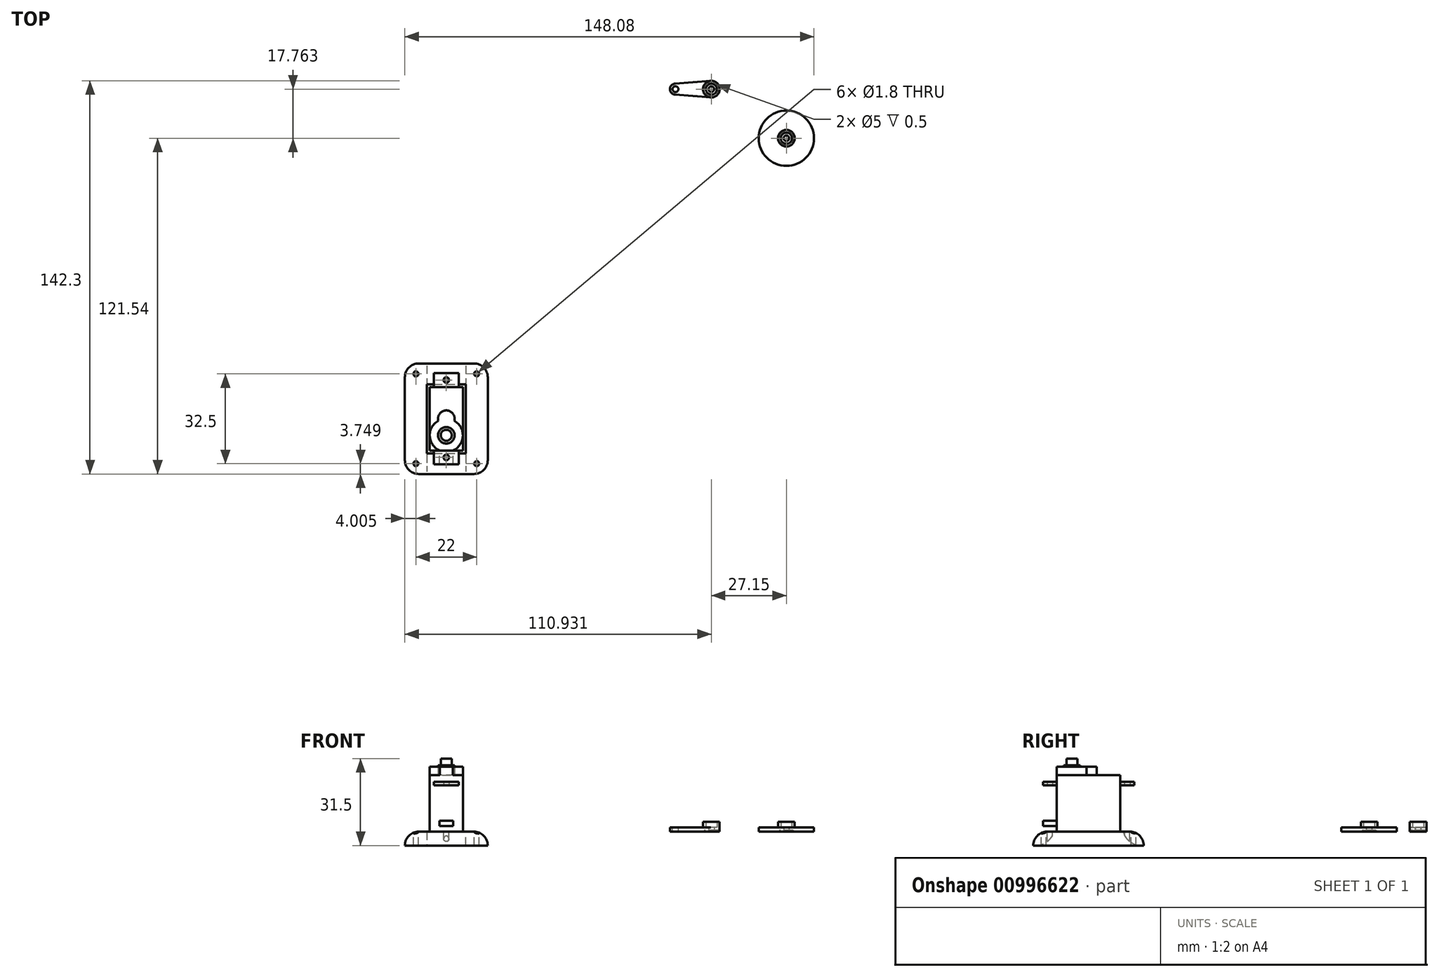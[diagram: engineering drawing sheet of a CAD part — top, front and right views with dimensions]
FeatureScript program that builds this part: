
annotation { "Feature Type Name" : "Feature", "Feature Type Description" : "" }
export const myFeature = defineFeature(function(context is Context, id is Id, definition is map)
    precondition{}
    {
        {
            var Q0;
            Q0=qCreatedBy(makeId("Top.planeOp"),FACE);
            var sketch = newSketch(context, id + "F0", { "sketchPlane" : qUnion([Q0])});
            skLineSegment(sketch, "E0.bottom", {"start": v(-62.64, -62.96) * mm, "end": v(-50.64, -62.96) * mm});
            skLineSegment(sketch, "E0.top", {"start": v(-62.64, -39.96) * mm, "end": v(-50.64, -39.96) * mm});
            skLineSegment(sketch, "E0.left", {"start": v(-62.64, -62.96) * mm, "end": v(-62.64, -39.96) * mm});
            skLineSegment(sketch, "E0.right", {"start": v(-50.64, -62.96) * mm, "end": v(-50.64, -39.96) * mm});
            skSolve(sketch);
        }
        {
            var Q0;
            Q0=makeQuery(id+"F0.imprint","IMPRINT",FACE,{"disambiguationData":[TD([[makeQuery(id+"F0.imprint","IMPRINT",EDGE,{"derivedFrom":sQuery(id+"F0.wireOp",EDGE,"E0.bottom")}),1.0]])]});
            extrude(context, id + "F1", {"entities" : qUnion([Q0]), "depth" : 20.5 * mm, "offsetDistance" : 25 * mm});
        }
        {
            var Q0;
            Q0=makeQuery(id+"F1.opExtrude","CAP_FACE",FACE,{"disambiguationData":[OSD([sQuery(id+"F0.wireOp",EDGE,"E0.bottom"),sQuery(id+"F0.wireOp",EDGE,"E0.top"),sQuery(id+"F0.wireOp",EDGE,"E0.left"),sQuery(id+"F0.wireOp",EDGE,"E0.right")])],"isStart":false});
            var sketch = newSketch(context, id + "F2", { "sketchPlane" : qUnion([Q0])});
            skLineSegment(sketch, "E1", {"start": v(-56.64, -39.96) * mm, "end": v(-56.64, -62.96) * mm, "construction": true});
            skCircle(sketch, "E2", {"center": v(-56.64, -57.46) * mm, "radius": 6 * mm});
            skArc(sketch, "E3", {"start": v(-53.73, -52.21) * mm, "mid": v(-56.64, -48.46) * mm, "end": v(-59.54, -52.21) * mm});
            skSolve(sketch);
        }
        {
            var Q0;
            {var subQ0=sQuery(id+"F2.wireOp",EDGE,"E2");var subQ4=sQuery(id+"F2.wireOp",EDGE,"E3");var subQ6=makeQuery(id+"F2.imprint","INTERSECT",VERTEX,{"disambiguationData":[OD(0.0)],"derivedFrom":[subQ0,subQ4]});Q0=makeQuery(id+"F2.imprint","IMPRINT",FACE,{"disambiguationData":[TD([[makeQuery(id+"F2.imprint","IMPRINT",EDGE,{"disambiguationData":[TD([[subQ6,1.0]])],"derivedFrom":subQ0}),1.0]])]});}
            var Q1;
            {var subQ0=sQuery(id+"F2.wireOp",EDGE,"E3");Q1=makeQuery(id+"F2.imprint","IMPRINT",FACE,{"disambiguationData":[TD([[makeQuery(id+"F2.imprint","IMPRINT",EDGE,{"derivedFrom":subQ0}),1.0]])]});}
            extrude(context, id + "F3", {"entities" : qUnion([Q0, Q1]), "operationType" : NewBodyOperationType.ADD, "depth" : 3 * mm, "offsetDistance" : 25 * mm});
        }
        {
            var Q0;
            Q0=makeQuery(id+"F3.opExtrude","CAP_FACE",FACE,{"disambiguationData":[OSD([sQuery(id+"F0.wireOp",EDGE,"E0.bottom"),sQuery(id+"F2.wireOp",EDGE,"E2"),sQuery(id+"F2.wireOp",EDGE,"E3")])],"isStart":false});
            var sketch = newSketch(context, id + "F4", { "sketchPlane" : qUnion([Q0])});
            skCircle(sketch, "E4", {"center": v(-56.64, -57.46) * mm, "radius": 3 * mm});
            skSolve(sketch);
        }
        {
            var Q0;
            Q0=makeQuery(id+"F4.imprint","IMPRINT",FACE,{"disambiguationData":[TD([[makeQuery(id+"F4.imprint","IMPRINT",EDGE,{"derivedFrom":sQuery(id+"F4.wireOp",EDGE,"E4")}),1.0]])]});
            extrude(context, id + "F5", {"entities" : qUnion([Q0]), "operationType" : NewBodyOperationType.ADD, "depth" : 0.5 * mm, "offsetDistance" : 25 * mm});
        }
        {
            var Q0;
            Q0=makeQuery(id+"F5.opExtrude","CAP_FACE",FACE,{"disambiguationData":[OSD([sQuery(id+"F4.wireOp",EDGE,"E4")])],"isStart":false});
            var sketch = newSketch(context, id + "F6", { "sketchPlane" : qUnion([Q0])});
            skCircle(sketch, "E5", {"center": v(-56.64, -57.46) * mm, "radius": 2 * mm});
            skSolve(sketch);
        }
        {
            var Q0;
            Q0=makeQuery(id+"F6.imprint","IMPRINT",FACE,{"disambiguationData":[TD([[makeQuery(id+"F6.imprint","IMPRINT",EDGE,{"derivedFrom":sQuery(id+"F6.wireOp",EDGE,"E5")}),1.0]])]});
            extrude(context, id + "F7", {"entities" : qUnion([Q0]), "operationType" : NewBodyOperationType.ADD, "depth" : 2.5 * mm, "offsetDistance" : 25 * mm});
        }
        {
            var Q0;
            Q0=qCreatedBy(makeId("Top.planeOp"),FACE);
            cPlane(context, id + "F8", {"entities" : qUnion([Q0]), "cplaneType" : CPlaneType.OFFSET, "offset" : 16.75 * mm, "width" : 150 * mm, "height" : 150 * mm});
        }
        {
            var Q0;
            Q0=qCreatedBy(id+"F8.planeOp",FACE);
            var sketch = newSketch(context, id + "F9", { "sketchPlane" : qUnion([Q0])});
            skLineSegment(sketch, "E6.bottom", {"start": v(-61.14, -62.96) * mm, "end": v(-52.14, -62.96) * mm});
            skLineSegment(sketch, "E6.top", {"start": v(-61.14, -67.96) * mm, "end": v(-52.14, -67.96) * mm});
            skLineSegment(sketch, "E6.left", {"start": v(-61.14, -62.96) * mm, "end": v(-61.14, -67.96) * mm});
            skLineSegment(sketch, "E6.right", {"start": v(-52.14, -62.96) * mm, "end": v(-52.14, -67.96) * mm});
            skLineSegment(sketch, "E7", {"start": v(-56.64, -62.96) * mm, "end": v(-56.64, -67.96) * mm, "construction": true});
            skLineSegment(sketch, "E8.bottom", {"start": v(-52.14, -34.96) * mm, "end": v(-61.14, -34.96) * mm});
            skLineSegment(sketch, "E8.top", {"start": v(-52.14, -39.96) * mm, "end": v(-61.14, -39.96) * mm});
            skLineSegment(sketch, "E8.left", {"start": v(-52.14, -34.96) * mm, "end": v(-52.14, -39.96) * mm});
            skLineSegment(sketch, "E8.right", {"start": v(-61.14, -34.96) * mm, "end": v(-61.14, -39.96) * mm});
            skLineSegment(sketch, "E9", {"start": v(-56.64, -39.96) * mm, "end": v(-56.64, -34.96) * mm, "construction": true});
            skCircle(sketch, "E10", {"center": v(-56.64, -37.46) * mm, "radius": 1 * mm});
            skCircle(sketch, "E11", {"center": v(-56.64, -65.46) * mm, "radius": 1 * mm});
            skSolve(sketch);
        }
        {
            var Q0;
            Q0=makeQuery(id+"F9.imprint","IMPRINT",FACE,{"disambiguationData":[TD([[makeQuery(id+"F9.imprint","IMPRINT",EDGE,{"derivedFrom":sQuery(id+"F9.wireOp",EDGE,"E6.bottom")}),-1.0]])]});
            var Q1;
            Q1=makeQuery(id+"F9.imprint","IMPRINT",FACE,{"disambiguationData":[TD([[makeQuery(id+"F9.imprint","IMPRINT",EDGE,{"derivedFrom":sQuery(id+"F9.wireOp",EDGE,"E8.bottom")}),1.0]])]});
            extrude(context, id + "F10", {"entities" : qUnion([Q0, Q1]), "operationType" : NewBodyOperationType.ADD, "depth" : 1.3 * mm, "offsetDistance" : 25 * mm});
        }
        {
            var Q0;
            {var subQ0=sQuery(id+"F0.wireOp",EDGE,"E0.bottom");Q0=makeQuery(id+"F3.boolean.opBoolean","MERGE",FACE,{"derivedFrom":[makeQuery(id+"F1.opExtrude","SWEPT_FACE",FACE,{"disambiguationData":[OSD([subQ0])]}),makeQuery(id+"F3.opExtrude","SWEPT_FACE",FACE,{"disambiguationData":[OSD([subQ0])]})]});}
            var sketch = newSketch(context, id + "F11", { "sketchPlane" : qUnion([Q0])});
            skLineSegment(sketch, "E12.bottom", {"start": v(-54.14, 4) * mm, "end": v(-59.14, 4) * mm});
            skLineSegment(sketch, "E12.top", {"start": v(-54.14, 2) * mm, "end": v(-59.14, 2) * mm});
            skLineSegment(sketch, "E12.left", {"start": v(-54.14, 4) * mm, "end": v(-54.14, 2) * mm});
            skLineSegment(sketch, "E12.right", {"start": v(-59.14, 4) * mm, "end": v(-59.14, 2) * mm});
            skLineSegment(sketch, "E13", {"start": v(-56.64, 4) * mm, "end": v(-56.64, 2) * mm, "construction": true});
            skSolve(sketch);
        }
        {
            var Q0;
            Q0=makeQuery(id+"F11.imprint","IMPRINT",FACE,{"disambiguationData":[TD([[makeQuery(id+"F11.imprint","IMPRINT",EDGE,{"derivedFrom":sQuery(id+"F11.wireOp",EDGE,"E12.bottom")}),1.0]])]});
            var Q1;
            Q1=makeQuery(id+"F10.opExtrude","SWEPT_FACE",FACE,{"disambiguationData":[OSD([sQuery(id+"F9.wireOp",EDGE,"E6.top")])]});
            extrude(context, id + "F12", {"entities" : qUnion([Q0]), "operationType" : NewBodyOperationType.ADD, "endBound" : BoundingType.UP_TO_SURFACE, "depth" : 25 * mm, "endBoundEntityFace" : qUnion([Q1]), "offsetDistance" : 25 * mm});
        }
        {
            var Q0;
            Q0=qCreatedBy(makeId("Top.planeOp"),FACE);
            var sketch = newSketch(context, id + "F13", { "sketchPlane" : qUnion([Q0])});
            skCircle(sketch, "E14", {"center": v(66.44, 50.08) * mm, "radius": 10 * mm});
            skCircle(sketch, "E15", {"center": v(66.44, 50.08) * mm, "radius": 2.5 * mm});
            skSolve(sketch);
        }
        {
            var Q0;
            Q0=makeQuery(id+"F13.imprint","IMPRINT",FACE,{"disambiguationData":[TD([[makeQuery(id+"F13.imprint","IMPRINT",EDGE,{"derivedFrom":sQuery(id+"F13.wireOp",EDGE,"E14")}),1.0]])]});
            extrude(context, id + "F14", {"entities" : qUnion([Q0]), "depth" : 0.5 * mm, "offsetDistance" : 25 * mm});
        }
        {
            var Q0;
            Q0=makeQuery(id+"F14.opExtrude","CAP_FACE",FACE,{"disambiguationData":[OSD([sQuery(id+"F13.wireOp",EDGE,"E14"),sQuery(id+"F13.wireOp",EDGE,"E15")])],"isStart":false});
            var sketch = newSketch(context, id + "F15", { "sketchPlane" : qUnion([Q0])});
            skCircle(sketch, "E16", {"center": v(66.44, 50.08) * mm, "radius": 1 * mm});
            skSolve(sketch);
        }
        {
            var Q0;
            Q0=makeQuery(id+"F15.imprint","IMPRINT",FACE,{"disambiguationData":[TD([[makeQuery(id+"F15.imprint","IMPRINT",EDGE,{"derivedFrom":makeQuery(id+"F14.opExtrude","CAP_EDGE",EDGE,{"disambiguationData":[OSD([sQuery(id+"F13.wireOp",EDGE,"E14")])],"isStart":false})}),1.0]])]});
            var Q1;
            Q1=makeQuery(id+"F15.imprint","IMPRINT",FACE,{"disambiguationData":[TD([[makeQuery(id+"F15.imprint","IMPRINT",EDGE,{"derivedFrom":sQuery(id+"F15.wireOp",EDGE,"E16")}),-1.0]])]});
            extrude(context, id + "F16", {"entities" : qUnion([Q0, Q1]), "operationType" : NewBodyOperationType.ADD, "depth" : 1.1 * mm, "offsetDistance" : 25 * mm});
        }
        {
            var Q0;
            Q0=makeQuery(id+"F16.opExtrude","CAP_FACE",FACE,{"disambiguationData":[OSD([sQuery(id+"F13.wireOp",EDGE,"E14"),sQuery(id+"F15.wireOp",EDGE,"E16")])],"isStart":false});
            var sketch = newSketch(context, id + "F17", { "sketchPlane" : qUnion([Q0])});
            skCircle(sketch, "E17", {"center": v(66.44, 50.08) * mm, "radius": 3 * mm});
            skCircle(sketch, "E18", {"center": v(66.44, 50.08) * mm, "radius": 2 * mm});
            skSolve(sketch);
        }
        {
            var Q0;
            Q0=makeQuery(id+"F17.imprint","IMPRINT",FACE,{"disambiguationData":[TD([[makeQuery(id+"F17.imprint","IMPRINT",EDGE,{"derivedFrom":sQuery(id+"F17.wireOp",EDGE,"E17")}),1.0]])]});
            extrude(context, id + "F18", {"entities" : qUnion([Q0]), "operationType" : NewBodyOperationType.ADD, "depth" : 2 * mm, "offsetDistance" : 25 * mm});
        }
        {
            var Q0;
            Q0=qCreatedBy(makeId("Top.planeOp"),FACE);
            var sketch = newSketch(context, id + "F19", { "sketchPlane" : qUnion([Q0])});
            skArc(sketch, "E19", {"start": v(39.06, 64.85) * mm, "mid": v(42.3, 67.84) * mm, "end": v(39.06, 70.83) * mm});
            skArc(sketch, "E20", {"start": v(26.14, 69.84) * mm, "mid": v(24.3, 67.84) * mm, "end": v(26.14, 65.85) * mm});
            skLineSegment(sketch, "E21", {"start": v(39.3, 67.84) * mm, "end": v(26.3, 67.84) * mm, "construction": true});
            skLineSegment(sketch, "E22", {"start": v(39.06, 64.85) * mm, "end": v(26.14, 65.85) * mm});
            skLineSegment(sketch, "E23", {"start": v(26.14, 69.84) * mm, "end": v(39.06, 70.83) * mm});
            skCircle(sketch, "E24", {"center": v(39.3, 67.84) * mm, "radius": 2.5 * mm});
            skSolve(sketch);
        }
        {
            var Q0;
            Q0=makeQuery(id+"F19.imprint","IMPRINT",FACE,{"disambiguationData":[TD([[makeQuery(id+"F19.imprint","IMPRINT",EDGE,{"derivedFrom":sQuery(id+"F19.wireOp",EDGE,"E19")}),1.0]])]});
            extrude(context, id + "F20", {"entities" : qUnion([Q0]), "depth" : 0.5 * mm, "offsetDistance" : 25 * mm});
        }
        {
            var Q0;
            Q0=makeQuery(id+"F20.opExtrude","CAP_FACE",FACE,{"disambiguationData":[OSD([sQuery(id+"F19.wireOp",EDGE,"E19"),sQuery(id+"F19.wireOp",EDGE,"E20"),sQuery(id+"F19.wireOp",EDGE,"E22"),sQuery(id+"F19.wireOp",EDGE,"E23"),sQuery(id+"F19.wireOp",EDGE,"E24")])],"isStart":false});
            var sketch = newSketch(context, id + "F21", { "sketchPlane" : qUnion([Q0])});
            skCircle(sketch, "E25", {"center": v(39.3, 67.84) * mm, "radius": 1 * mm});
            skSolve(sketch);
        }
        {
            var Q0;
            Q0=makeQuery(id+"F21.imprint","IMPRINT",FACE,{"disambiguationData":[TD([[makeQuery(id+"F21.imprint","IMPRINT",EDGE,{"derivedFrom":sQuery(id+"F21.wireOp",EDGE,"E25")}),-1.0]])]});
            var sketch = newSketch(context, id + "F22", { "sketchPlane" : qUnion([Q0])});
            skSolve(sketch);
        }
        {
            var Q0;
            Q0=makeQuery(id+"F22.imprint","IMPRINT",FACE,{"disambiguationData":[TD([[makeQuery(id+"F22.imprint","IMPRINT",EDGE,{"derivedFrom":makeQuery(id+"F21.imprint","IMPRINT",EDGE,{"derivedFrom":sQuery(id+"F21.wireOp",EDGE,"E25")})}),-1.0]])]});
            var Q1;
            Q1=makeQuery(id+"F21.imprint","IMPRINT",FACE,{"disambiguationData":[TD([[makeQuery(id+"F21.imprint","IMPRINT",EDGE,{"derivedFrom":makeQuery(id+"F20.opExtrude","CAP_EDGE",EDGE,{"disambiguationData":[OSD([sQuery(id+"F19.wireOp",EDGE,"E19")])],"isStart":false})}),1.0]])]});
            extrude(context, id + "F23", {"entities" : qUnion([Q0, Q1]), "operationType" : NewBodyOperationType.ADD, "depth" : 1.1 * mm, "offsetDistance" : 25 * mm});
        }
        {
            var Q0;
            {var subQ0=sQuery(id+"F19.wireOp",EDGE,"E24");Q0=makeQuery(id+"F23.boolean.opBoolean","MERGE",FACE,{"derivedFrom":[makeQuery(id+"F23.opExtrude","CAP_FACE",FACE,{"disambiguationData":[OSD([sQuery(id+"F19.wireOp",EDGE,"E19"),sQuery(id+"F19.wireOp",EDGE,"E20"),sQuery(id+"F19.wireOp",EDGE,"E22"),sQuery(id+"F19.wireOp",EDGE,"E23"),subQ0])],"isStart":false}),makeQuery(id+"F23.opExtrude","CAP_FACE",FACE,{"disambiguationData":[OSD([subQ0,sQuery(id+"F21.wireOp",EDGE,"E25")])],"isStart":false})]});}
            var sketch = newSketch(context, id + "F24", { "sketchPlane" : qUnion([Q0])});
            skCircle(sketch, "E26", {"center": v(39.3, 67.84) * mm, "radius": 2 * mm});
            skCircle(sketch, "E27", {"center": v(39.3, 67.84) * mm, "radius": 3 * mm});
            skSolve(sketch);
        }
        {
            var Q0;
            Q0=makeQuery(id+"F24.imprint","IMPRINT",FACE,{"disambiguationData":[TD([[makeQuery(id+"F24.imprint","IMPRINT",EDGE,{"derivedFrom":sQuery(id+"F24.wireOp",EDGE,"E26")}),-1.0]])]});
            extrude(context, id + "F25", {"entities" : qUnion([Q0]), "operationType" : NewBodyOperationType.ADD, "depth" : 2 * mm, "offsetDistance" : 25 * mm});
        }
        {
            var Q0;
            {var subQ0=sQuery(id+"F19.wireOp",EDGE,"E22");var subQ1=sQuery(id+"F19.wireOp",EDGE,"E20");var subQ2=sQuery(id+"F19.wireOp",EDGE,"E23");var subQ3=sQuery(id+"F19.wireOp",EDGE,"E19");var subQ4=sQuery(id+"F19.wireOp",EDGE,"E24");Q0=makeQuery(id+"F25.boolean.opBoolean","SPLIT",FACE,{"disambiguationData":[TD([makeQuery(id+"F20.opExtrude","SWEPT_FACE",FACE,{"disambiguationData":[OSD([subQ3])]})])],"derivedFrom":makeQuery(id+"F23.boolean.opBoolean","MERGE",FACE,{"derivedFrom":[makeQuery(id+"F23.opExtrude","CAP_FACE",FACE,{"disambiguationData":[OSD([subQ3,subQ1,subQ0,subQ2,subQ4])],"isStart":false}),makeQuery(id+"F23.opExtrude","CAP_FACE",FACE,{"disambiguationData":[OSD([subQ4,sQuery(id+"F21.wireOp",EDGE,"E25")])],"isStart":false})]})});}
            var sketch = newSketch(context, id + "F26", { "sketchPlane" : qUnion([Q0])});
            skCircle(sketch, "E28", {"center": v(26.3, 67.84) * mm, "radius": 1.05 * mm});
            skSolve(sketch);
        }
        {
            var Q0;
            Q0=makeQuery(id+"F26.imprint","IMPRINT",FACE,{"disambiguationData":[TD([[makeQuery(id+"F26.imprint","IMPRINT",EDGE,{"derivedFrom":sQuery(id+"F26.wireOp",EDGE,"E28")}),1.0]])]});
            extrude(context, id + "F27", {"entities" : qUnion([Q0]), "operationType" : NewBodyOperationType.REMOVE, "endBound" : BoundingType.THROUGH_ALL, "oppositeDirection" : true, "depth" : 25 * mm, "offsetDistance" : 25 * mm});
        }
        {
            var Q0;
            Q0=makeQuery(id+"F1.opExtrude","CAP_FACE",FACE,{"disambiguationData":[OSD([sQuery(id+"F0.wireOp",EDGE,"E0.bottom"),sQuery(id+"F0.wireOp",EDGE,"E0.top"),sQuery(id+"F0.wireOp",EDGE,"E0.left"),sQuery(id+"F0.wireOp",EDGE,"E0.right")])],"isStart":true});
            var sketch = newSketch(context, id + "F28", { "sketchPlane" : qUnion([Q0])});
            skLineSegment(sketch, "E29.bottom", {"start": v(-71.64, 71.46) * mm, "end": v(-41.64, 71.46) * mm});
            skLineSegment(sketch, "E29.top", {"start": v(-71.64, 31.46) * mm, "end": v(-41.64, 31.46) * mm});
            skLineSegment(sketch, "E29.left", {"start": v(-71.64, 71.46) * mm, "end": v(-71.64, 31.46) * mm});
            skLineSegment(sketch, "E29.right", {"start": v(-41.64, 71.46) * mm, "end": v(-41.64, 31.46) * mm});
            skLineSegment(sketch, "E30", {"start": v(-71.64, 51.46) * mm, "end": v(-41.64, 51.46) * mm, "construction": true});
            skLineSegment(sketch, "E31", {"start": v(-56.64, 51.46) * mm, "end": v(-56.64, 71.46) * mm, "construction": true});
            skLineSegment(sketch, "E32", {"start": v(-62.64, 51.46) * mm, "end": v(-50.64, 51.46) * mm, "construction": true});
            skLineSegment(sketch, "E33", {"start": v(-50.64, 51.46) * mm, "end": v(-56.64, 51.46) * mm, "construction": true});
            skLineSegment(sketch, "E34", {"start": v(-56.64, 51.46) * mm, "end": v(-56.64, 39.96) * mm, "construction": true});
            skCircle(sketch, "E35", {"center": v(-56.64, 37.46) * mm, "radius": 0.9 * mm});
            skCircle(sketch, "E36", {"center": v(-56.64, 65.46) * mm, "radius": 0.9 * mm});
            skLineSegment(sketch, "E37.bottom", {"start": v(-63.64, 38.96) * mm, "end": v(-49.64, 38.96) * mm});
            skLineSegment(sketch, "E37.top", {"start": v(-63.64, 63.96) * mm, "end": v(-49.64, 63.96) * mm});
            skLineSegment(sketch, "E37.left", {"start": v(-63.64, 38.96) * mm, "end": v(-63.64, 63.96) * mm});
            skLineSegment(sketch, "E37.right", {"start": v(-49.64, 38.96) * mm, "end": v(-49.64, 63.96) * mm});
            skLineSegment(sketch, "E38", {"start": v(-71.64, 31.46) * mm, "end": v(-63.64, 38.96) * mm, "construction": true});
            skLineSegment(sketch, "E39", {"start": v(-63.64, 63.96) * mm, "end": v(-71.64, 71.46) * mm, "construction": true});
            skLineSegment(sketch, "E40", {"start": v(-49.64, 63.96) * mm, "end": v(-41.64, 71.46) * mm, "construction": true});
            skLineSegment(sketch, "E41", {"start": v(-49.64, 38.96) * mm, "end": v(-41.64, 31.46) * mm, "construction": true});
            skCircle(sketch, "E42", {"center": v(-67.64, 67.71) * mm, "radius": 0.9 * mm});
            skCircle(sketch, "E43", {"center": v(-45.64, 67.71) * mm, "radius": 0.9 * mm});
            skCircle(sketch, "E44", {"center": v(-45.64, 35.21) * mm, "radius": 0.9 * mm});
            skCircle(sketch, "E45", {"center": v(-67.64, 35.21) * mm, "radius": 0.9 * mm});
            skSolve(sketch);
        }
        {
            var Q0;
            Q0=makeQuery(id+"F28.imprint","IMPRINT",FACE,{"disambiguationData":[TD([[makeQuery(id+"F28.imprint","IMPRINT",EDGE,{"derivedFrom":sQuery(id+"F28.wireOp",EDGE,"E29.bottom")}),-1.0]])]});
            extrude(context, id + "F29", {"entities" : qUnion([Q0]), "depth" : 5 * mm, "offsetDistance" : 25 * mm});
        }
        {
            var Q0;
            Q0=makeQuery(id+"F29.opExtrude","CAP_EDGE",EDGE,{"disambiguationData":[OSD([sQuery(id+"F28.wireOp",EDGE,"E29.bottom")])],"isStart":true});
            var Q1;
            Q1=makeQuery(id+"F29.opExtrude","CAP_EDGE",EDGE,{"disambiguationData":[OSD([sQuery(id+"F28.wireOp",EDGE,"E29.left")])],"isStart":true});
            var Q2;
            Q2=makeQuery(id+"F29.opExtrude","CAP_EDGE",EDGE,{"disambiguationData":[OSD([sQuery(id+"F28.wireOp",EDGE,"E29.top")])],"isStart":true});
            var Q3;
            Q3=makeQuery(id+"F29.opExtrude","CAP_EDGE",EDGE,{"disambiguationData":[OSD([sQuery(id+"F28.wireOp",EDGE,"E29.right")])],"isStart":true});
            var Q4;
            Q4=makeQuery(id+"F29.opExtrude","SWEPT_EDGE",EDGE,{"disambiguationData":[OSD([sQuery(id+"F28.wireOp",EDGE,"E29.bottom"),sQuery(id+"F28.wireOp",EDGE,"E29.left")])]});
            var Q5;
            Q5=makeQuery(id+"F29.opExtrude","SWEPT_EDGE",EDGE,{"disambiguationData":[OSD([sQuery(id+"F28.wireOp",EDGE,"E29.bottom"),sQuery(id+"F28.wireOp",EDGE,"E29.right")])]});
            var Q6;
            Q6=makeQuery(id+"F29.opExtrude","SWEPT_EDGE",EDGE,{"disambiguationData":[OSD([sQuery(id+"F28.wireOp",EDGE,"E29.top"),sQuery(id+"F28.wireOp",EDGE,"E29.right")])]});
            var Q7;
            Q7=makeQuery(id+"F29.opExtrude","SWEPT_EDGE",EDGE,{"disambiguationData":[OSD([sQuery(id+"F28.wireOp",EDGE,"E29.top"),sQuery(id+"F28.wireOp",EDGE,"E29.left")])]});
            fillet(context, id + "F30", {"entities" : qUnion([Q0, Q1, Q2, Q3, Q4, Q5, Q6, Q7]), "radius" : 5 * mm, "tangentPropagation" : true, "allowEdgeOverflow" : false});
        }
        {
            var Q0;
            Q0=makeQuery(id+"F29.opExtrude","CAP_EDGE",EDGE,{"disambiguationData":[OSD([sQuery(id+"F28.wireOp",EDGE,"E37.top")])],"isStart":false});
            var Q1;
            Q1=makeQuery(id+"F29.opExtrude","CAP_EDGE",EDGE,{"disambiguationData":[OSD([sQuery(id+"F28.wireOp",EDGE,"E37.bottom")])],"isStart":false});
            fillet(context, id + "F31", {"entities" : qUnion([Q0, Q1]), "radius" : 7 * mm, "tangentPropagation" : true, "allowEdgeOverflow" : false});
        }
    });
